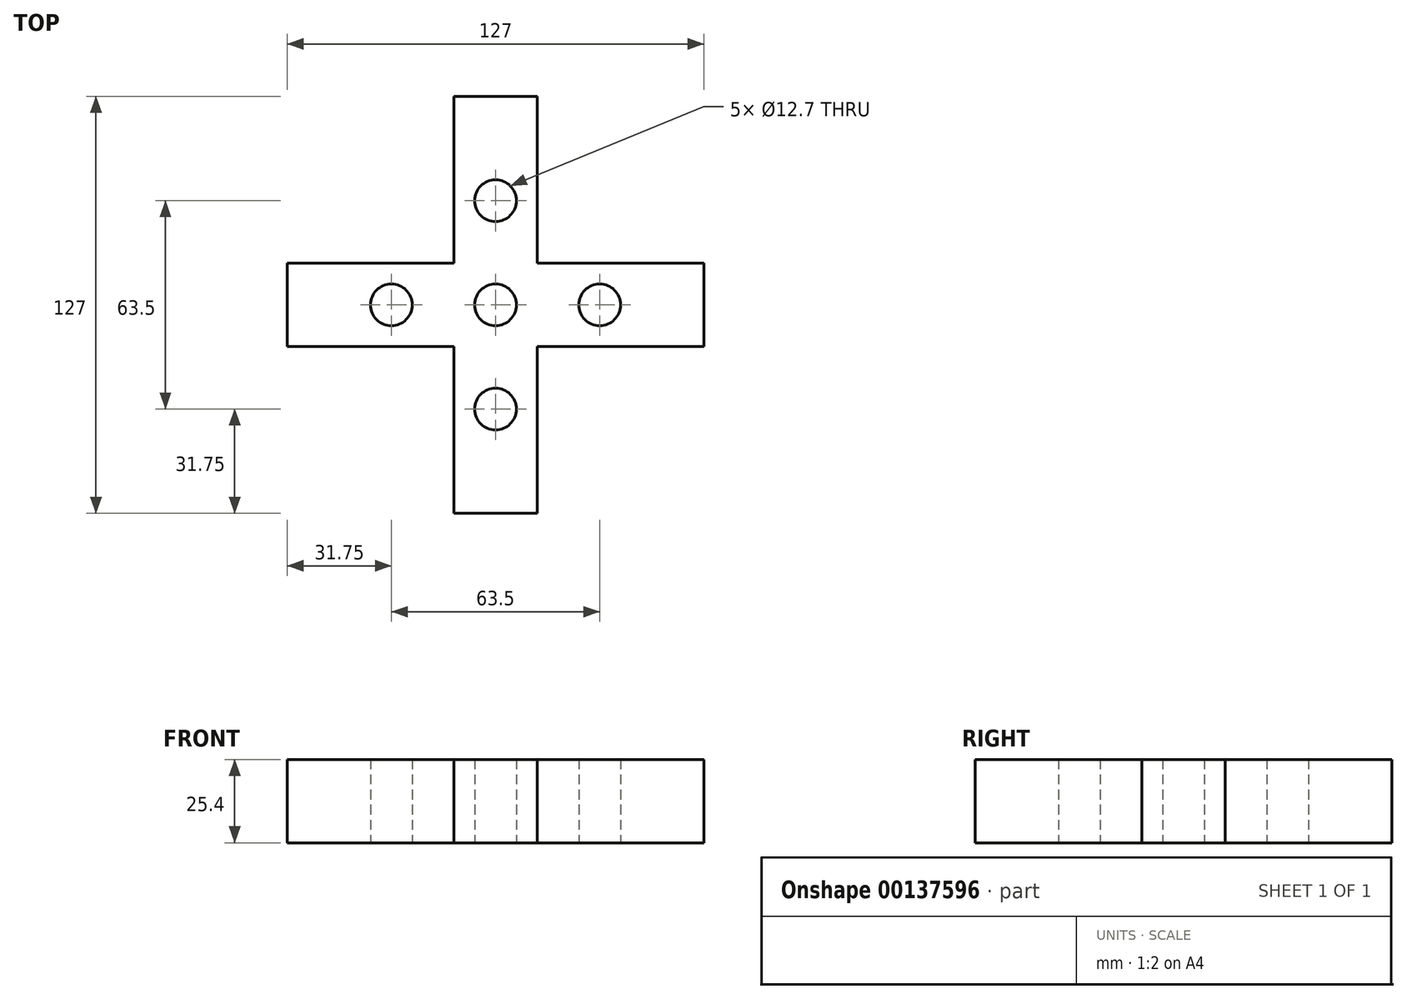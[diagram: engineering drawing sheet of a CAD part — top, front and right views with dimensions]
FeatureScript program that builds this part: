
annotation { "Feature Type Name" : "Feature", "Feature Type Description" : "" }
export const myFeature = defineFeature(function(context is Context, id is Id, definition is map)
    precondition{}
    {
        {
            var Q0;
            Q0=qCreatedBy(makeId("Top.planeOp"),FACE);
            var sketch = newSketch(context, id + "F0", { "sketchPlane" : qUnion([Q0])});
            skLineSegment(sketch, "E0.bottom", {"start": v(63.5, -12.7) * mm, "end": v(-63.5, -12.7) * mm});
            skLineSegment(sketch, "E0.top", {"start": v(63.5, 12.7) * mm, "end": v(-63.5, 12.7) * mm});
            skLineSegment(sketch, "E0.left", {"start": v(63.5, -12.7) * mm, "end": v(63.5, 12.7) * mm});
            skLineSegment(sketch, "E0.right", {"start": v(-63.5, -12.7) * mm, "end": v(-63.5, 12.7) * mm});
            skPoint(sketch, "E0.middle", {"position": v(0, 0) * mm});
            skLineSegment(sketch, "E1.bottom", {"start": v(12.7, -63.5) * mm, "end": v(-12.7, -63.5) * mm});
            skLineSegment(sketch, "E1.top", {"start": v(12.7, 63.5) * mm, "end": v(-12.7, 63.5) * mm});
            skLineSegment(sketch, "E1.left", {"start": v(12.7, -63.5) * mm, "end": v(12.7, 63.5) * mm});
            skLineSegment(sketch, "E1.right", {"start": v(-12.7, -63.5) * mm, "end": v(-12.7, 63.5) * mm});
            skLineSegment(sketch, "E2.bottom", {"start": v(12.7, -12.7) * mm, "end": v(-12.7, -12.7) * mm});
            skLineSegment(sketch, "E2.top", {"start": v(12.7, 12.7) * mm, "end": v(-12.7, 12.7) * mm});
            skLineSegment(sketch, "E2.left", {"start": v(12.7, -12.7) * mm, "end": v(12.7, 12.7) * mm});
            skLineSegment(sketch, "E2.right", {"start": v(-12.7, -12.7) * mm, "end": v(-12.7, 12.7) * mm});
            skLineSegment(sketch, "E3", {"start": v(0, -63.5) * mm, "end": v(0, 0) * mm});
            skLineSegment(sketch, "E4", {"start": v(0, 0) * mm, "end": v(0, 63.5) * mm});
            skLineSegment(sketch, "E5", {"start": v(0, 63.5) * mm, "end": v(0, 0) * mm});
            skLineSegment(sketch, "E6", {"start": v(0, 0) * mm, "end": v(-63.5, 0) * mm});
            skLineSegment(sketch, "E7", {"start": v(0, 0) * mm, "end": v(63.5, 0) * mm});
            skPoint(sketch, "E8", {"position": v(0, -31.75) * mm});
            skPoint(sketch, "E9", {"position": v(31.75, 0) * mm});
            skPoint(sketch, "E10", {"position": v(0, 31.75) * mm});
            skPoint(sketch, "E11", {"position": v(-31.75, 0) * mm});
            skSolve(sketch);
        }
        {
            var Q0;
            Q0 = qSketchRegion(id + "F0", true);
            var Q1;
            {var subQ1=sQuery(id+"F0.wireOp",EDGE,"E2.top");var subQ3=sQuery(id+"F0.wireOp",EDGE,"E5");var subQ4=makeQuery(id+"F0.imprint","INTERSECT",VERTEX,{"derivedFrom":[subQ1,subQ3]});Q1=makeQuery(id+"F0.imprint","IMPRINT",FACE,{"disambiguationData":[TD([[makeQuery(id+"F0.imprint","IMPRINT",EDGE,{"disambiguationData":[TD([[subQ4,1.0]])],"derivedFrom":subQ1}),1.0]])]});}
            var Q2;
            {var subQ1=sQuery(id+"F0.wireOp",EDGE,"E2.top");var subQ3=sQuery(id+"F0.wireOp",EDGE,"E5");var subQ4=makeQuery(id+"F0.imprint","INTERSECT",VERTEX,{"derivedFrom":[subQ1,subQ3]});Q2=makeQuery(id+"F0.imprint","IMPRINT",FACE,{"disambiguationData":[TD([[makeQuery(id+"F0.imprint","IMPRINT",EDGE,{"disambiguationData":[TD([[subQ4,-1.0]])],"derivedFrom":subQ1}),1.0]])]});}
            extrude(context, id + "F1", {"entities" : qUnion([Q0, Q1, Q2]), "depth" : 25.4 * mm});
        }
        {
            var Q0;
            Q0=sQuery(id+"F0.wireOp",VERTEX,"E9");
            var Q1;
            Q1=sQuery(id+"F0.wireOp",VERTEX,"E10");
            var Q2;
            Q2=sQuery(id+"F0.wireOp",VERTEX,"E11");
            var Q3;
            Q3=sQuery(id+"F0.wireOp",VERTEX,"E0.middle");
            var Q4;
            Q4=sQuery(id+"F0.wireOp",VERTEX,"E8");
            var Q5;
            Q5=makeQuery(id+"F1.opExtrude","SWEPT_BODY",BODY,{"disambiguationData":[OSD([sQuery(id+"F0.wireOp",EDGE,"E0.bottom"),sQuery(id+"F0.wireOp",EDGE,"E0.top"),sQuery(id+"F0.wireOp",EDGE,"E0.left"),sQuery(id+"F0.wireOp",EDGE,"E0.right"),sQuery(id+"F0.wireOp",EDGE,"E1.bottom"),sQuery(id+"F0.wireOp",EDGE,"E1.top"),sQuery(id+"F0.wireOp",EDGE,"E1.left"),sQuery(id+"F0.wireOp",EDGE,"E1.right")])]});
            hole(context, id + "F2", {"style" : HoleStyle.SIMPLE, "endStyle" : HoleEndStyle.THROUGH, "oppositeDirection" : true, "holeDiameter" : 12.7 * mm, "startFromSketch" : true, "locations" : qUnion([Q0, Q1, Q2, Q3, Q4]), "scope" : qUnion([Q5]), "isTappedThrough" : true});
        }
    });
